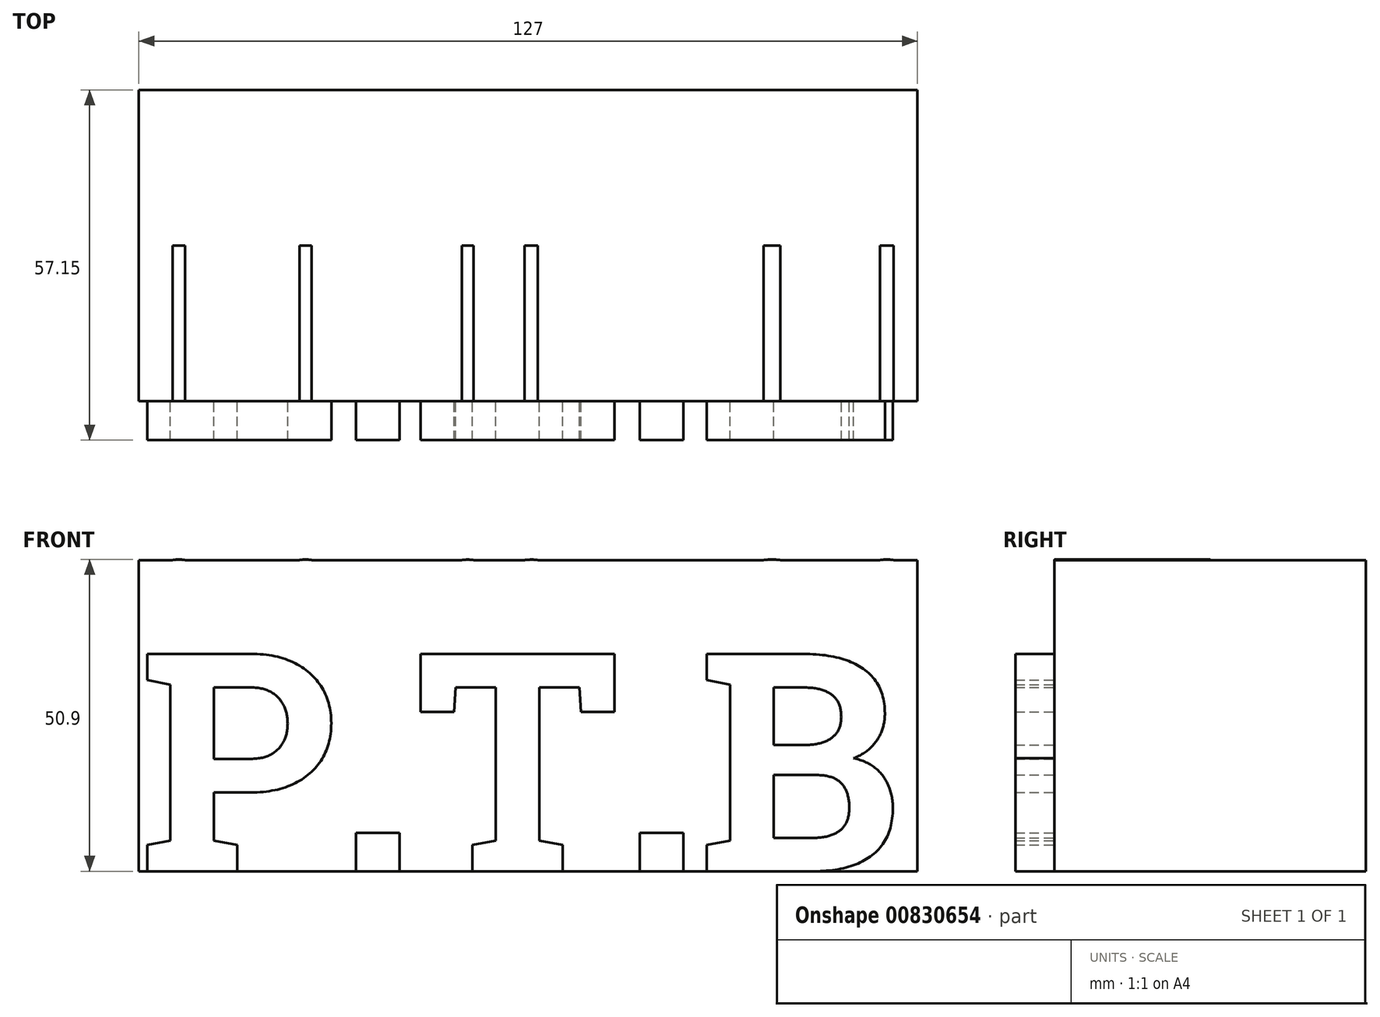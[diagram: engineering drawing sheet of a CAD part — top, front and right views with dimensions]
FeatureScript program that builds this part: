
annotation { "Feature Type Name" : "Feature", "Feature Type Description" : "" }
export const myFeature = defineFeature(function(context is Context, id is Id, definition is map)
    precondition{}
    {
        {
            var Q0;
            Q0=qCreatedBy(makeId("Front.planeOp"),FACE);
            var sketch = newSketch(context, id + "F0", { "sketchPlane" : qUnion([Q0])});
            skLineSegment(sketch, "E0.bottom", {"start": v(0, 0) * mm, "end": v(127, 0) * mm});
            skLineSegment(sketch, "E0.top", {"start": v(0, 50.8) * mm, "end": v(127, 50.8) * mm});
            skLineSegment(sketch, "E0.left", {"start": v(0, 0) * mm, "end": v(0, 50.8) * mm});
            skLineSegment(sketch, "E0.right", {"start": v(127, 0) * mm, "end": v(127, 50.8) * mm});
            skSolve(sketch);
        }
        {
            var Q0;
            Q0=makeQuery(id+"F0.imprint","IMPRINT",FACE,{"disambiguationData":[TD([[makeQuery(id+"F0.imprint","IMPRINT",EDGE,{"derivedFrom":sQuery(id+"F0.wireOp",EDGE,"E0.bottom")}),1.0]])]});
            extrude(context, id + "F1", {"entities" : qUnion([Q0]), "oppositeDirection" : true, "depth" : 25.4 * mm, "offsetDistance" : 25.4 * mm});
        }
        {
            var Q0;
            Q0=makeQuery(id+"F1.opExtrude","CAP_FACE",FACE,{"disambiguationData":[OSD([sQuery(id+"F0.wireOp",EDGE,"E0.bottom"),sQuery(id+"F0.wireOp",EDGE,"E0.top"),sQuery(id+"F0.wireOp",EDGE,"E0.left"),sQuery(id+"F0.wireOp",EDGE,"E0.right")])],"isStart":true});
            var sketch = newSketch(context, id + "F2", { "sketchPlane" : qUnion([Q0])});
            skText(sketch, "E1", { "text": "P.T.B", "fontName": "RobotoSlab-Bold.ttf"});
            const initialGuessF2  = {"E1": [0, 0, 1, 0, 0.03593]};
            skSetInitialGuess(sketch, initialGuessF2);
            skSolve(sketch);
        }
        {
            var Q0;
            Q0=makeQuery(id+"F2.imprint","IMPRINT",FACE,{"disambiguationData":[TD([[makeQuery(id+"F2.imprint","IMPRINT",EDGE,{"derivedFrom":sQuery(id+"F2.wireOp",EDGE,"E1.sketch_text.stroke-0")}),-1.0]])]});
            var Q1;
            Q1=makeQuery(id+"F2.imprint","IMPRINT",FACE,{"disambiguationData":[TD([[makeQuery(id+"F2.imprint","IMPRINT",EDGE,{"derivedFrom":sQuery(id+"F2.wireOp",EDGE,"E1.sketch_text.stroke-27")}),-1.0]])]});
            var Q2;
            Q2=makeQuery(id+"F2.imprint","IMPRINT",FACE,{"disambiguationData":[TD([[makeQuery(id+"F2.imprint","IMPRINT",EDGE,{"derivedFrom":sQuery(id+"F2.wireOp",EDGE,"E1.sketch_text.stroke-47")}),-1.0]])]});
            var Q3;
            Q3=makeQuery(id+"F2.imprint","IMPRINT",FACE,{"disambiguationData":[TD([[makeQuery(id+"F2.imprint","IMPRINT",EDGE,{"derivedFrom":sQuery(id+"F2.wireOp",EDGE,"E1.sketch_text.stroke-43")}),1.0]])]});
            var Q4;
            Q4=makeQuery(id+"F2.imprint","IMPRINT",FACE,{"disambiguationData":[TD([[makeQuery(id+"F2.imprint","IMPRINT",EDGE,{"derivedFrom":sQuery(id+"F2.wireOp",EDGE,"E1.sketch_text.stroke-23")}),1.0]])]});
            var Q5;
            Q5=makeQuery(id+"F1.opExtrude","CAP_FACE",FACE,{"disambiguationData":[OSD([sQuery(id+"F0.wireOp",EDGE,"E0.bottom"),sQuery(id+"F0.wireOp",EDGE,"E0.top"),sQuery(id+"F0.wireOp",EDGE,"E0.left"),sQuery(id+"F0.wireOp",EDGE,"E0.right")])],"isStart":false});
            extrude(context, id + "F3", {"entities" : qUnion([Q0, Q1, Q2, Q3, Q4, Q5]), "operationType" : NewBodyOperationType.ADD, "depth" : 6.35 * mm, "offsetDistance" : 25.4 * mm});
        }
        {
            var Q0;
            {var subQ0=sQuery(id+"F0.wireOp",EDGE,"E0.bottom");var subQ1=sQuery(id+"F0.wireOp",EDGE,"E0.right");var subQ2=sQuery(id+"F0.wireOp",EDGE,"E0.top");var subQ3=sQuery(id+"F0.wireOp",EDGE,"E0.left");Q0=makeQuery(id+"F3.boolean.opBoolean","SPLIT",FACE,{"disambiguationData":[TD([makeQuery(id+"F1.opExtrude","SWEPT_FACE",FACE,{"disambiguationData":[OSD([subQ0])]})])],"derivedFrom":makeQuery(id+"F1.opExtrude","CAP_FACE",FACE,{"disambiguationData":[OSD([subQ0,subQ2,subQ3,subQ1])],"isStart":true})});}
            var sketch = newSketch(context, id + "F4", { "sketchPlane" : qUnion([Q0])});
            skText(sketch, "E2", { "text": "010-1234-5678", "fontName": "OpenSans-BoldItalic.ttf"});
            const initialGuessF4  = {"E2": [0, 0.03729, 1, 0, 0.01351]};
            skSetInitialGuess(sketch, initialGuessF4);
            skSolve(sketch);
        }
        {
            var Q0;
            Q0 = qSketchRegion(id + "F4", true);
            var Q1;
            Q1=makeQuery(id+"F1.opExtrude","CAP_FACE",FACE,{"disambiguationData":[OSD([sQuery(id+"F0.wireOp",EDGE,"E0.bottom"),sQuery(id+"F0.wireOp",EDGE,"E0.top"),sQuery(id+"F0.wireOp",EDGE,"E0.left"),sQuery(id+"F0.wireOp",EDGE,"E0.right")])],"isStart":false});
            extrude(context, id + "F5", {"entities" : qUnion([Q0, Q1]), "operationType" : NewBodyOperationType.ADD, "depth" : -25.4 * mm, "offsetDistance" : 25.4 * mm});
        }
    });
